# Revit family: ONSTAR LED
name_source: partatom
category: Lighting Fixtures
revit_build: Autodesk Revit Architecture 2015 (Build: 20140322_1515(x64)
units: mm (PartAtom-declared; Revit-internal decimal feet)

## types (1)
- KANLUX ONSTAR LED-GR 22760 LED 6500K 60lm tworzywo ABS szary
    Apparent Load = 2 VA
    Color Filter = 16777215
    Default Elevation = 0 mm  [stored 0 ft]
    Dimming Lamp Color Temperature Shift = <None>
    Długość = 230 mm
    IP = IP65
    Klasyfikacja obciążenia = Oświetlenie
    Kod = 22760
    Lamp = LED
    Manufacturer = KANLUX
    Masa = 0.22 kg
    Materiał klosz = KANLUX - klosz - poliwęglan (PC)
    Materiał obudowa = KANLUX - obudowa - tworzywo ABS, szary
    Moc oprawy = 2 W
    Model = ONSTAR LED-GR
    Photometric Web File = ONSTAR_LED-GR.ies
    Szerokość = 78 mm  [stored 0.255906 ft]
    Tilt Angle = 90.00°
    URL = www.kanlux.pl
    Wattage Comments = 1.7
    Współczynnik mocy = 1
    Wysokość = 20 mm  [stored 0.0656168 ft]

note: [stored X ft] marks values corroborated as IEEE doubles in the binary element streams (Revit-internal decimal feet)
